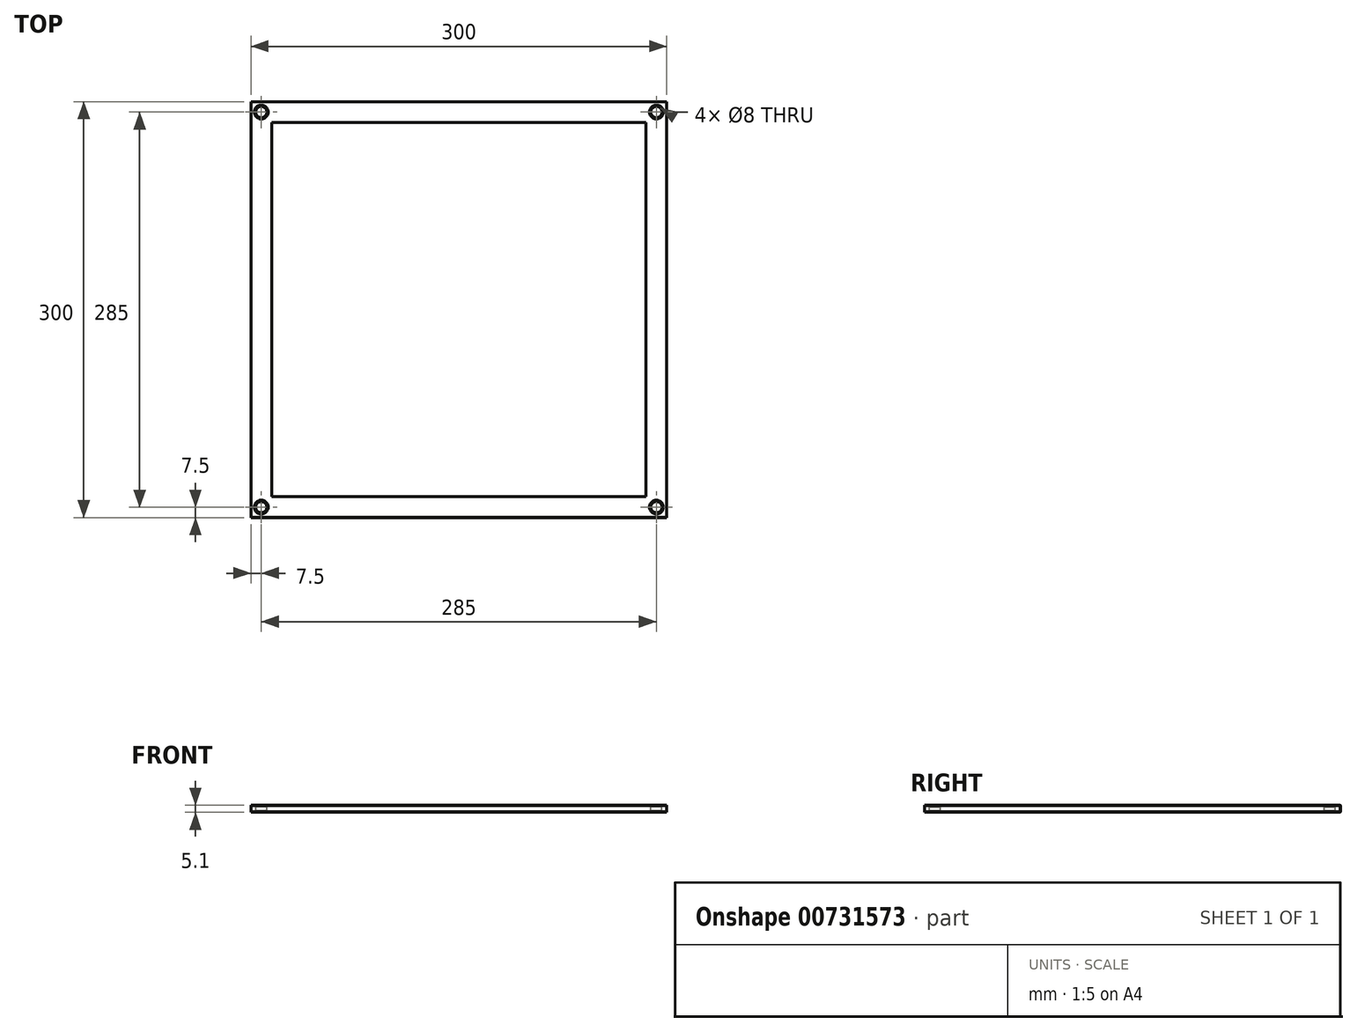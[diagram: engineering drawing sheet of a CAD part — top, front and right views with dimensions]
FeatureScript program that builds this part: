
annotation { "Feature Type Name" : "Feature", "Feature Type Description" : "" }
export const myFeature = defineFeature(function(context is Context, id is Id, definition is map)
    precondition{}
    {
        {
            var Q0;
            Q0=qCreatedBy(makeId("Top.planeOp"),FACE);
            var sketch = newSketch(context, id + "F0", { "sketchPlane" : qUnion([Q0])});
            skCircle(sketch, "E0.cCircle", {"center": v(0, 0) * mm, "radius": 150 * mm, "construction": true});
            skLineSegment(sketch, "E0.0", {"start": v(150, -150) * mm, "end": v(-150, -150) * mm});
            skLineSegment(sketch, "E0.1", {"start": v(-150, -150) * mm, "end": v(-150, 150) * mm});
            skLineSegment(sketch, "E0.2", {"start": v(-150, 150) * mm, "end": v(150, 150) * mm});
            skLineSegment(sketch, "E0.3", {"start": v(150, 150) * mm, "end": v(150, -150) * mm});
            skPoint(sketch, "E0.0.midPoint", {"position": v(0, -150) * mm});
            skSolve(sketch);
        }
        {
            var Q0;
            Q0 = qSketchRegion(id + "F0", true);
            extrude(context, id + "F1", {"entities" : qUnion([Q0]), "depth" : 5 * mm, "offsetDistance" : 25 * mm});
        }
        {
            var Q0;
            Q0=makeQuery(id+"F1.opExtrude","CAP_FACE",FACE,{"disambiguationData":[OSD([sQuery(id+"F0.wireOp",EDGE,"E0.0"),sQuery(id+"F0.wireOp",EDGE,"E0.1"),sQuery(id+"F0.wireOp",EDGE,"E0.2"),sQuery(id+"F0.wireOp",EDGE,"E0.3")])],"isStart":false});
            var Q1;
            Q1=makeQuery(id+"F1.opExtrude","CAP_FACE",FACE,{"disambiguationData":[OSD([sQuery(id+"F0.wireOp",EDGE,"E0.0"),sQuery(id+"F0.wireOp",EDGE,"E0.1"),sQuery(id+"F0.wireOp",EDGE,"E0.2"),sQuery(id+"F0.wireOp",EDGE,"E0.3")])],"isStart":true});
            var Q2;
            Q2=makeQuery(id+"F1.opExtrude","SWEPT_EDGE",EDGE,{"disambiguationData":[OSD([sQuery(id+"F0.wireOp",EDGE,"E0.0"),sQuery(id+"F0.wireOp",EDGE,"E0.1")])]});
            var Q3;
            Q3=makeQuery(id+"F1.opExtrude","SWEPT_EDGE",EDGE,{"disambiguationData":[OSD([sQuery(id+"F0.wireOp",EDGE,"E0.0"),sQuery(id+"F0.wireOp",EDGE,"E0.3")])]});
            var Q4;
            Q4=makeQuery(id+"F1.opExtrude","SWEPT_EDGE",EDGE,{"disambiguationData":[OSD([sQuery(id+"F0.wireOp",EDGE,"E0.2"),sQuery(id+"F0.wireOp",EDGE,"E0.3")])]});
            var Q5;
            Q5=makeQuery(id+"F1.opExtrude","SWEPT_EDGE",EDGE,{"disambiguationData":[OSD([sQuery(id+"F0.wireOp",EDGE,"E0.1"),sQuery(id+"F0.wireOp",EDGE,"E0.2")])]});
            chamfer(context, id + "F2", {"entities" : qUnion([Q0, Q1, Q2, Q3, Q4, Q5]), "width" : 0.25 * mm, "tangentPropagation" : true});
        }
        {
            var Q0;
            Q0=makeQuery(id+"F1.opExtrude","CAP_FACE",FACE,{"disambiguationData":[OSD([sQuery(id+"F0.wireOp",EDGE,"E0.0"),sQuery(id+"F0.wireOp",EDGE,"E0.1"),sQuery(id+"F0.wireOp",EDGE,"E0.2"),sQuery(id+"F0.wireOp",EDGE,"E0.3")])],"isStart":false});
            var sketch = newSketch(context, id + "F3", { "sketchPlane" : qUnion([Q0])});
            skCircle(sketch, "E1.cCircle", {"center": v(0, 0) * mm, "radius": 135 * mm, "construction": true});
            skLineSegment(sketch, "E1.0", {"start": v(135, -135) * mm, "end": v(-135, -135) * mm});
            skLineSegment(sketch, "E1.1", {"start": v(-135, -135) * mm, "end": v(-135, 135) * mm});
            skLineSegment(sketch, "E1.2", {"start": v(-135, 135) * mm, "end": v(135, 135) * mm});
            skLineSegment(sketch, "E1.3", {"start": v(135, 135) * mm, "end": v(135, -135) * mm});
            skPoint(sketch, "E1.0.midPoint", {"position": v(0, -135) * mm});
            skSolve(sketch);
        }
        {
            var Q0;
            Q0 = qSketchRegion(id + "F3", true);
            extrude(context, id + "F4", {"entities" : qUnion([Q0]), "depth" : 0.1 * mm, "offsetDistance" : 25 * mm});
        }
        {
            var Q0;
            Q0=makeQuery(id+"F1.opExtrude","CAP_FACE",FACE,{"disambiguationData":[OSD([sQuery(id+"F0.wireOp",EDGE,"E0.0"),sQuery(id+"F0.wireOp",EDGE,"E0.1"),sQuery(id+"F0.wireOp",EDGE,"E0.2"),sQuery(id+"F0.wireOp",EDGE,"E0.3")])],"isStart":false});
            var sketch = newSketch(context, id + "F5", { "sketchPlane" : qUnion([Q0])});
            skLineSegment(sketch, "E2.bottom", {"start": v(-135, 135) * mm, "end": v(-150, 135) * mm, "construction": true});
            skLineSegment(sketch, "E2.top", {"start": v(-135, 150) * mm, "end": v(-150, 150) * mm, "construction": true});
            skLineSegment(sketch, "E2.left", {"start": v(-135, 135) * mm, "end": v(-135, 150) * mm, "construction": true});
            skLineSegment(sketch, "E2.right", {"start": v(-150, 135) * mm, "end": v(-150, 150) * mm, "construction": true});
            skLineSegment(sketch, "E3", {"start": v(-150, 142.5) * mm, "end": v(-135, 142.5) * mm, "construction": true});
            skLineSegment(sketch, "E4", {"start": v(-142.5, 135) * mm, "end": v(-142.5, 150) * mm, "construction": true});
            skCircle(sketch, "E5", {"center": v(-142.5, 142.5) * mm, "radius": 4 * mm});
            skLineSegment(sketch, "E6.1.0", {"start": v(135, 142.5) * mm, "end": v(150, 142.5) * mm, "construction": true});
            skCircle(sketch, "E6.1.1", {"center": v(142.5, 142.5) * mm, "radius": 4 * mm});
            skLineSegment(sketch, "E6.1.2", {"start": v(142.5, 150) * mm, "end": v(142.5, 135) * mm, "construction": true});
            skLineSegment(sketch, "E6.1.3", {"start": v(135, 135) * mm, "end": v(150, 135) * mm, "construction": true});
            skLineSegment(sketch, "E6.1.4", {"start": v(135, 135) * mm, "end": v(135, 150) * mm, "construction": true});
            skLineSegment(sketch, "E6.1.5", {"start": v(135, 150) * mm, "end": v(150, 150) * mm, "construction": true});
            skLineSegment(sketch, "E6.1.6", {"start": v(150, 135) * mm, "end": v(150, 150) * mm, "construction": true});
            skLineSegment(sketch, "E6.2.0", {"start": v(142.5, -135) * mm, "end": v(142.5, -150) * mm, "construction": true});
            skCircle(sketch, "E6.2.1", {"center": v(142.5, -142.5) * mm, "radius": 4 * mm});
            skLineSegment(sketch, "E6.2.2", {"start": v(150, -142.5) * mm, "end": v(135, -142.5) * mm, "construction": true});
            skLineSegment(sketch, "E6.2.3", {"start": v(135, -135) * mm, "end": v(135, -150) * mm, "construction": true});
            skLineSegment(sketch, "E6.2.4", {"start": v(135, -135) * mm, "end": v(150, -135) * mm, "construction": true});
            skLineSegment(sketch, "E6.2.5", {"start": v(150, -135) * mm, "end": v(150, -150) * mm, "construction": true});
            skLineSegment(sketch, "E6.2.6", {"start": v(135, -150) * mm, "end": v(150, -150) * mm, "construction": true});
            skLineSegment(sketch, "E6.3.0", {"start": v(-135, -142.5) * mm, "end": v(-150, -142.5) * mm, "construction": true});
            skCircle(sketch, "E6.3.1", {"center": v(-142.5, -142.5) * mm, "radius": 4 * mm});
            skLineSegment(sketch, "E6.3.2", {"start": v(-142.5, -150) * mm, "end": v(-142.5, -135) * mm, "construction": true});
            skLineSegment(sketch, "E6.3.3", {"start": v(-135, -135) * mm, "end": v(-150, -135) * mm, "construction": true});
            skLineSegment(sketch, "E6.3.4", {"start": v(-135, -135) * mm, "end": v(-135, -150) * mm, "construction": true});
            skLineSegment(sketch, "E6.3.5", {"start": v(-135, -150) * mm, "end": v(-150, -150) * mm, "construction": true});
            skLineSegment(sketch, "E6.3.6", {"start": v(-150, -135) * mm, "end": v(-150, -150) * mm, "construction": true});
            skPoint(sketch, "E6.center", {"position": v(0, 0) * mm});
            skLineSegment(sketch, "E6.anchor1", {"start": v(0, 0) * mm, "end": v(-142.5, 135) * mm, "construction": true});
            skLineSegment(sketch, "E6.anchor2", {"start": v(0, 0) * mm, "end": v(-135, -142.5) * mm, "construction": true});
            skSolve(sketch);
        }
        {
            var Q0;
            Q0 = qSketchRegion(id + "F5", true);
            extrude(context, id + "F6", {"entities" : qUnion([Q0]), "operationType" : NewBodyOperationType.REMOVE, "oppositeDirection" : true, "depth" : 25 * mm, "offsetDistance" : 25 * mm});
        }
        {
            var Q0;
            Q0=makeQuery(id+"F6.boolean.opBoolean","COPY",FACE,{"derivedFrom":makeQuery(id+"F6.opExtrude","SWEPT_FACE",FACE,{"disambiguationData":[OSD([sQuery(id+"F5.wireOp",EDGE,"E5")])]})});
            var Q1;
            Q1=makeQuery(id+"F6.boolean.opBoolean","COPY",FACE,{"derivedFrom":makeQuery(id+"F6.opExtrude","SWEPT_FACE",FACE,{"disambiguationData":[OSD([sQuery(id+"F5.wireOp",EDGE,"E6.3.1")])]})});
            var Q2;
            Q2=makeQuery(id+"F6.boolean.opBoolean","COPY",FACE,{"derivedFrom":makeQuery(id+"F6.opExtrude","SWEPT_FACE",FACE,{"disambiguationData":[OSD([sQuery(id+"F5.wireOp",EDGE,"E6.2.1")])]})});
            var Q3;
            Q3=makeQuery(id+"F6.boolean.opBoolean","COPY",FACE,{"derivedFrom":makeQuery(id+"F6.opExtrude","SWEPT_FACE",FACE,{"disambiguationData":[OSD([sQuery(id+"F5.wireOp",EDGE,"E6.1.1")])]})});
            chamfer(context, id + "F7", {"entities" : qUnion([Q0, Q1, Q2, Q3]), "width" : 1 * mm, "tangentPropagation" : true});
        }
    });
